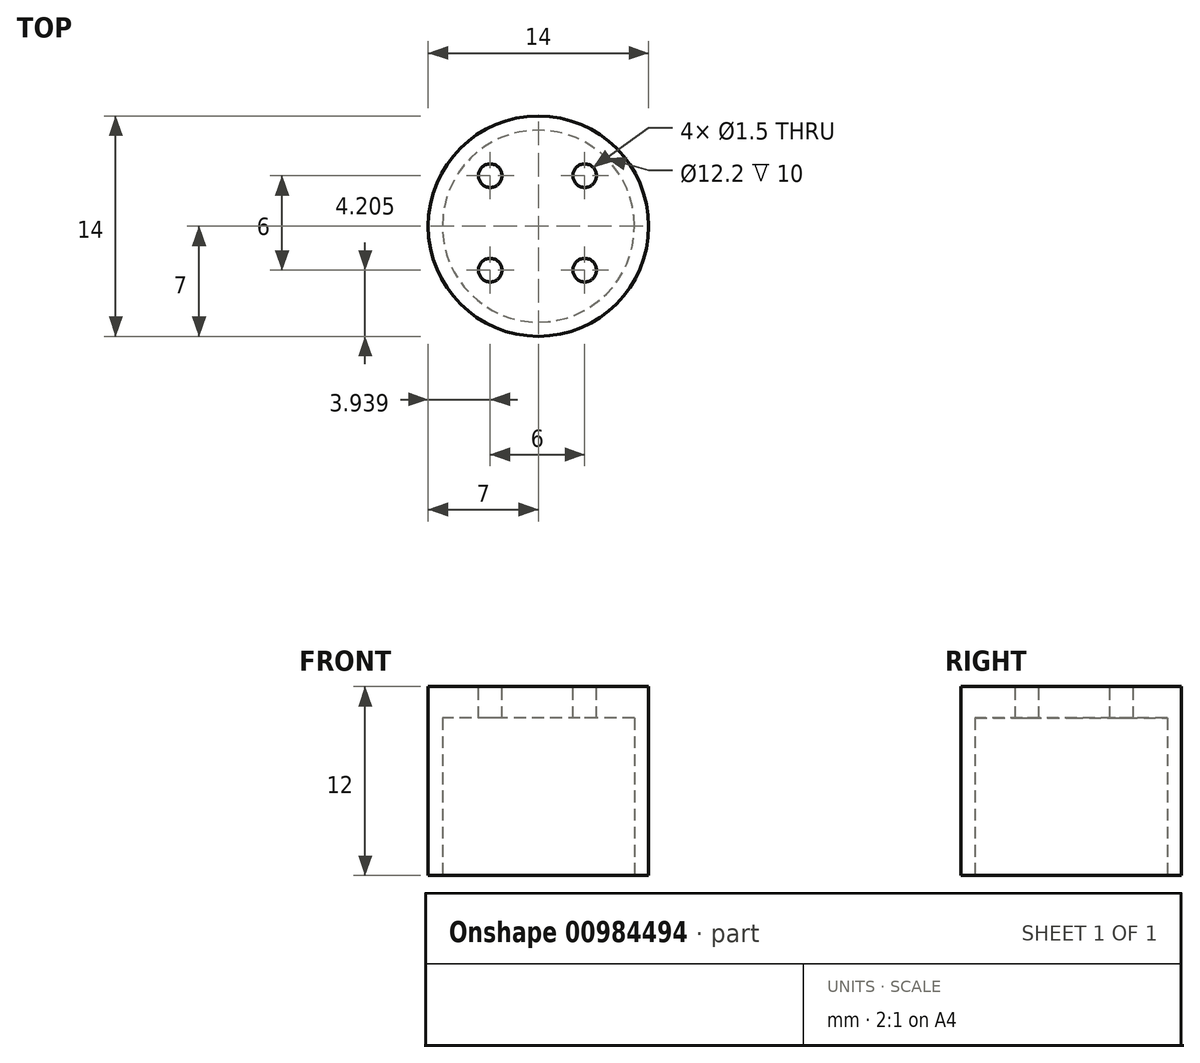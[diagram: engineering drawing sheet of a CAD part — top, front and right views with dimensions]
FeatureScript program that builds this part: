
annotation { "Feature Type Name" : "Feature", "Feature Type Description" : "" }
export const myFeature = defineFeature(function(context is Context, id is Id, definition is map)
    precondition{}
    {
        {
            var Q0;
            Q0=qCreatedBy(makeId("Top.planeOp"),FACE);
            var sketch = newSketch(context, id + "F0", { "sketchPlane" : qUnion([Q0])});
            skCircle(sketch, "E0", {"center": v(0, 0) * mm, "radius": 6.1 * mm});
            skCircle(sketch, "E1", {"center": v(0, 0) * mm, "radius": 7 * mm});
            skSolve(sketch);
        }
        {
            var Q0;
            Q0=qSketchRegion(id+"F0",true);
            extrude(context, id + "F1", {"entities" : qUnion([Q0]), "depth" : 10 * mm, "offsetDistance" : 25 * mm});
        }
        {
            var Q0;
            Q0=makeQuery(id+"F1.opExtrude","CAP_FACE",FACE,{"disambiguationData":[OSD([sQuery(id+"F0.wireOp",EDGE,"E0"),sQuery(id+"F0.wireOp",EDGE,"E1")])],"isStart":false});
            var sketch = newSketch(context, id + "F2", { "sketchPlane" : qUnion([Q0])});
            skCircle(sketch, "E2", {"center": v(0, 0) * mm, "radius": 7 * mm});
            skSolve(sketch);
        }
        {
            var Q0;
            Q0=qSketchRegion(id+"F2",true);
            extrude(context, id + "F3", {"entities" : qUnion([Q0]), "operationType" : NewBodyOperationType.ADD, "depth" : 2 * mm, "offsetDistance" : 25 * mm});
        }
        {
            var Q0;
            Q0=makeQuery(id+"F3.opExtrude","CAP_FACE",FACE,{"disambiguationData":[OSD([sQuery(id+"F2.wireOp",EDGE,"E2")])],"isStart":false});
            var sketch = newSketch(context, id + "F4", { "sketchPlane" : qUnion([Q0])});
            skCircle(sketch, "E3", {"center": v(2.94, -2.8) * mm, "radius": 0.75 * mm});
            skCircle(sketch, "E4.0.1.0", {"center": v(2.94, 3.2) * mm, "radius": 0.75 * mm});
            skCircle(sketch, "E4.1.0.0", {"center": v(-3.06, -2.8) * mm, "radius": 0.75 * mm});
            skCircle(sketch, "E4.1.1.0", {"center": v(-3.06, 3.2) * mm, "radius": 0.75 * mm});
            skLineSegment(sketch, "E4.direction1", {"start": v(2.94, -2.8) * mm, "end": v(-3.06, -2.8) * mm, "construction": true});
            skLineSegment(sketch, "E4.direction2", {"start": v(2.94, -2.8) * mm, "end": v(2.94, 3.2) * mm, "construction": true});
            skSolve(sketch);
        }
        {
            var Q0;
            Q0=qSketchRegion(id+"F4",true);
            var Q1;
            Q1=makeQuery(id+"F3.opExtrude","CAP_FACE",FACE,{"disambiguationData":[OSD([sQuery(id+"F2.wireOp",EDGE,"E2")])],"isStart":true});
            extrude(context, id + "F5", {"entities" : qUnion([Q0]), "operationType" : NewBodyOperationType.REMOVE, "endBound" : BoundingType.UP_TO_SURFACE, "oppositeDirection" : true, "depth" : 25 * mm, "endBoundEntityFace" : qUnion([Q1]), "offsetDistance" : 25 * mm});
        }
    });
